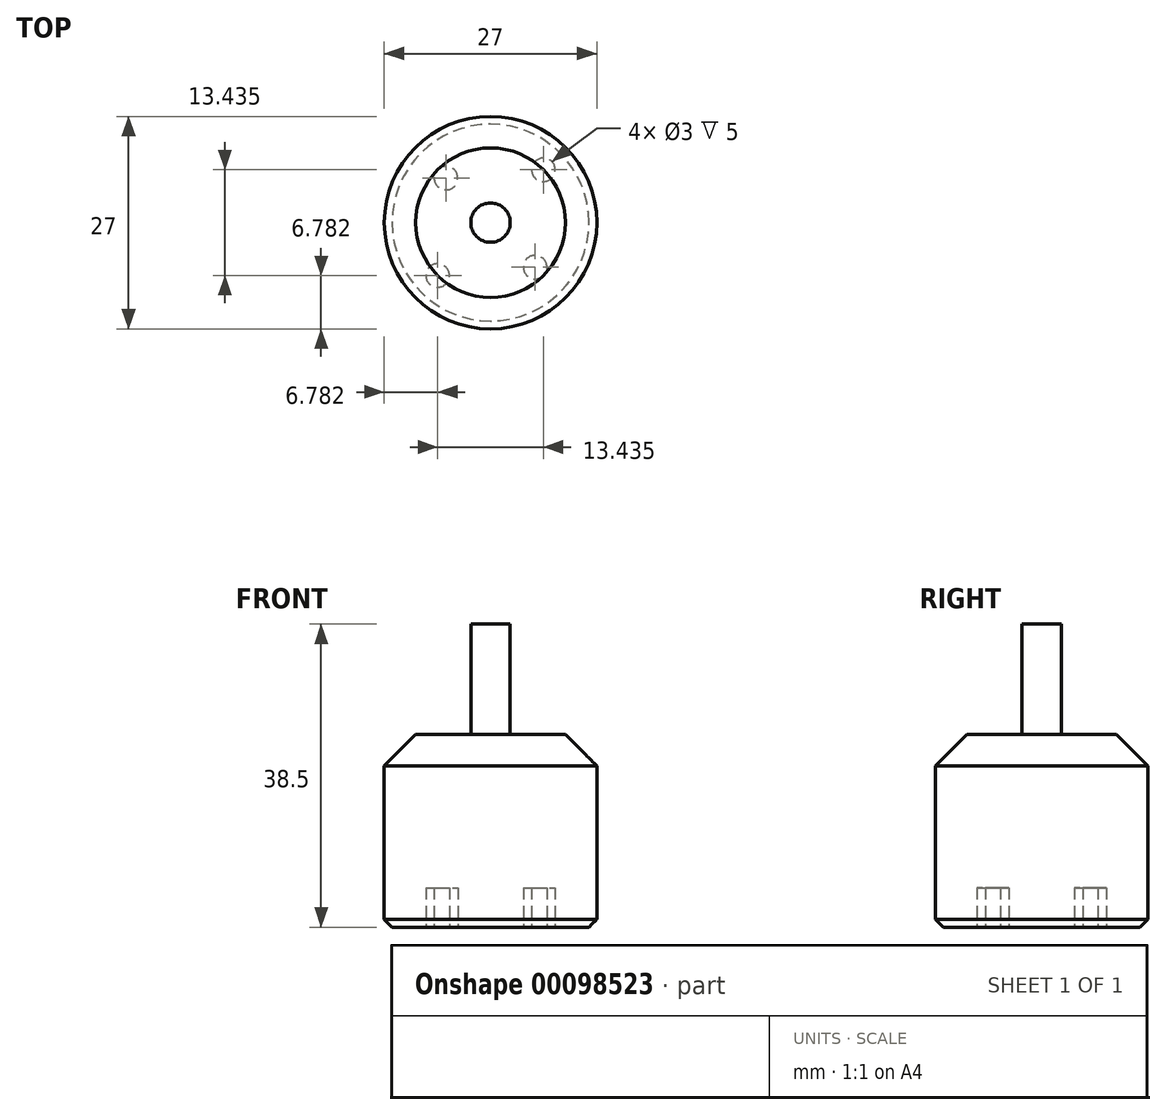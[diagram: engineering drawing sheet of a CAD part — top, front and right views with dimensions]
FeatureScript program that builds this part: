
annotation { "Feature Type Name" : "Feature", "Feature Type Description" : "" }
export const myFeature = defineFeature(function(context is Context, id is Id, definition is map)
    precondition{}
    {
        {
            var Q0;
            Q0=qCreatedBy(makeId("Top.planeOp"),FACE);
            var sketch = newSketch(context, id + "F0", { "sketchPlane" : qUnion([Q0])});
            skCircle(sketch, "E0", {"center": v(0, 0) * mm, "radius": 13.5 * mm});
            skSolve(sketch);
        }
        {
            var Q0;
            Q0 = qSketchRegion(id + "F0", true);
            extrude(context, id + "F1", {"entities" : qUnion([Q0]), "depth" : 24.5 * mm});
        }
        {
            var Q0;
            Q0=makeQuery(id+"F1.opExtrude","CAP_FACE",FACE,{"disambiguationData":[OSD([sQuery(id+"F0.wireOp",EDGE,"E0")])],"isStart":false});
            var sketch = newSketch(context, id + "F2", { "sketchPlane" : qUnion([Q0])});
            skCircle(sketch, "E1", {"center": v(0, 0) * mm, "radius": 2.5 * mm});
            skSolve(sketch);
        }
        {
            var Q0;
            Q0=makeQuery(id+"F2.imprint","IMPRINT",FACE,{"disambiguationData":[TD([[makeQuery(id+"F2.imprint","IMPRINT",EDGE,{"derivedFrom":sQuery(id+"F2.wireOp",EDGE,"E1")}),1.0]])]});
            extrude(context, id + "F3", {"entities" : qUnion([Q0]), "operationType" : NewBodyOperationType.ADD, "depth" : 14 * mm});
        }
        {
            var Q0;
            Q0=makeQuery(id+"F1.opExtrude","CAP_FACE",FACE,{"disambiguationData":[OSD([sQuery(id+"F0.wireOp",EDGE,"E0")])],"isStart":true});
            var sketch = newSketch(context, id + "F4", { "sketchPlane" : qUnion([Q0])});
            skLineSegment(sketch, "E2", {"start": v(0, 0) * mm, "end": v(5.66, 5.66) * mm});
            skLineSegment(sketch, "E3", {"start": v(0, 0) * mm, "end": v(-5.66, -5.66) * mm});
            skLineSegment(sketch, "E4", {"start": v(0, 0) * mm, "end": v(6.72, -6.72) * mm});
            skLineSegment(sketch, "E5", {"start": v(0, 0) * mm, "end": v(-6.72, 6.72) * mm});
            skCircle(sketch, "E6", {"center": v(5.66, 5.66) * mm, "radius": 1.5 * mm});
            skCircle(sketch, "E7", {"center": v(6.72, -6.72) * mm, "radius": 1.5 * mm});
            skCircle(sketch, "E8", {"center": v(-5.66, -5.66) * mm, "radius": 1.5 * mm});
            skCircle(sketch, "E9", {"center": v(-6.72, 6.72) * mm, "radius": 1.5 * mm});
            skSolve(sketch);
        }
        {
            var Q0;
            Q0=makeQuery(id+"F4.imprint","IMPRINT",FACE,{"disambiguationData":[TD([[makeQuery(id+"F4.imprint","IMPRINT",EDGE,{"derivedFrom":sQuery(id+"F4.wireOp",EDGE,"E7")}),1.0]])]});
            var Q1;
            Q1=makeQuery(id+"F4.imprint","IMPRINT",FACE,{"disambiguationData":[TD([[makeQuery(id+"F4.imprint","IMPRINT",EDGE,{"derivedFrom":sQuery(id+"F4.wireOp",EDGE,"E9")}),1.0]])]});
            var Q2;
            Q2=makeQuery(id+"F4.imprint","IMPRINT",FACE,{"disambiguationData":[TD([[makeQuery(id+"F4.imprint","IMPRINT",EDGE,{"derivedFrom":sQuery(id+"F4.wireOp",EDGE,"E6")}),1.0]])]});
            var Q3;
            Q3=makeQuery(id+"F4.imprint","IMPRINT",FACE,{"disambiguationData":[TD([[makeQuery(id+"F4.imprint","IMPRINT",EDGE,{"derivedFrom":sQuery(id+"F4.wireOp",EDGE,"E8")}),1.0]])]});
            extrude(context, id + "F5", {"entities" : qUnion([Q0, Q1, Q2, Q3]), "operationType" : NewBodyOperationType.REMOVE, "oppositeDirection" : true, "depth" : 5 * mm});
        }
        {
            var Q0;
            Q0=makeQuery(id+"F1.opExtrude","CAP_EDGE",EDGE,{"disambiguationData":[OSD([sQuery(id+"F0.wireOp",EDGE,"E0")])],"isStart":true});
            chamfer(context, id + "F6", {"entities" : qUnion([Q0]), "width" : 1 * mm, "tangentPropagation" : true});
        }
        {
            var Q0;
            Q0=makeQuery(id+"F1.opExtrude","CAP_EDGE",EDGE,{"disambiguationData":[OSD([sQuery(id+"F0.wireOp",EDGE,"E0")])],"isStart":false});
            chamfer(context, id + "F7", {"entities" : qUnion([Q0]), "width" : 4 * mm, "tangentPropagation" : true});
        }
    });
